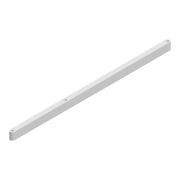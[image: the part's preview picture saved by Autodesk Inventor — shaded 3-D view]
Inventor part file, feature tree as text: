
AUTODESK INVENTOR PART (.ipt)
format: ipt  version: 2022 (Build 260153000, 153)  size: 90,112 bytes
history: native  units: mm
features: extrude x1, sketch x1
ambient origin geometry x8: Origin, YZ Plane, XZ Plane, XY Plane, X Axis, Y Axis, Z Axis, Center Point
bodies: Solid1 (feature_tree)
feature tree (2):
  extrude  "Extrusion1"  Depth=212.266mm
  sketch  "Sketch1"  dims[d0=6.0mm d1=212.266mm d2=3.0mm d3=3.0mm d4=10.0mm d5=0.0mm d10=3.0mm d11=72.721mm]
